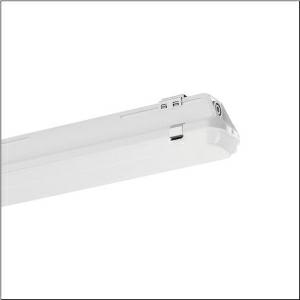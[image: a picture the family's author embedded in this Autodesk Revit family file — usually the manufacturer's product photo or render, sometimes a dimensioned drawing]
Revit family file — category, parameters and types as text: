
# Revit family: monsun_r__12_51fp10tp960x_8af5
name_source: partatom
category: Lighting Fixtures
units: mm (PartAtom-declared; Revit-internal decimal feet)

## family parameters
Cut with Voids When Loaded = No
Host = Face
Light Source = No
Part Type = Normal
Room Calculation Point = No
Round Connector Dimension = Use Diameter
Shared = No

## types (1)
- --- (1 x LED 2700 K ... 6500 K, 6010 lm, 36.8 W, 6500K)
    Apparent Load = 37 VA
    CIE Flux Codes = 47 76 93 94 100
    Color Rendering = 80
    Color Temperature = 6500K
    Default Elevation = 1800 mm
    Description = Monsun® 12, damp-proof luminaire, chain hanger, primary optical cover: enclosure, of PMMA, light emission: direct distribution, primary light characteristic: symmetric, installation type: suspended mounting, surface-mounted, horizontal mounting, vertical mounting, LED rated luminous flux: 5.980 lm, light colour: 8tw, colour temperature: 2700..6500K, control gear: ECG DALI, with terminal, 5-pole, max. 2.5mm², mains connection: 220..240V, AC, 50/60Hz, rated input power: 37W, luminaire housing, of glass-fibre reinforced polyester, uncoated, bright grey, length: 1.590 mm, width: 90 mm, height: 88mm, clip for enclosure, of stainless steel (V2A), ceiling mounting element, of stainless steel (V2A), chain hanger, of stainless steel (V2A), protection rating (complete): IP66, insulation class (complete): insulation class I (protective earthing), certification: CE, ENEC, VDE, protection symbol: D, impact resistance: IK04, permissible ambient temperature for indoor applications: -25..+35°C, standard: EN 50419, EN 60598-2-1, no direct snow, no direct sun, no direct rain, for indoor or canopied outdoor use, corresponds to IFS (International Featured Standards) requirements for safety and quality in the food industry, for animal farming (ammonia tested): for use in cowhouse, pig house, horse-stables... (not for use in poultry stables), AT max for animal farming = 40°C, packaging unit: 1 piece
    Height = 89 mm
    Lamp = 1 x LED 2700 K ... 6500 K
    Lamp Light Flux = 6010 lm
    Lamp Power = 36.8 W
    Lamp count = 1
    Length = 1590 mm
    Luminous efficacy = 163 lm/W
    Manufacturer = Siteco
    ModVariant = No
    Model = 51FP10TP960X
    Mounting Place = Ceiling
    Mounting Type = Pendant
    Number of Poles = 1
    OnlyDefault = Yes
    Power Factor = 1
    Product Name = Monsun® 12
    Product group = damp-proof luminaire | ceiling pendant
    ProductGroupID = 908
    Protection Class = Protection class I
    Protection Degree = IP 66
    RLX_Detail_Level = 1
    RlxData = <blob elided: 89045 chars, md5=928f6a14>
    Socket = socket
    Standby Power = 0 W
    System Light Flux = 6010 lm
    System Power = 37 W
    Type Comments = individual setting: CCT=6500K
    Type Image = l_1004748.jpg
    URL = http://relux.com
    VarID = @adj_135555
    Voltage = 0 V
    Weight = 0.00 kg
    Width = 90 mm

## geometry (parser evidence)
native form markers: Blend x4, Sweep x16
no freeform markers — native parametric forms only
